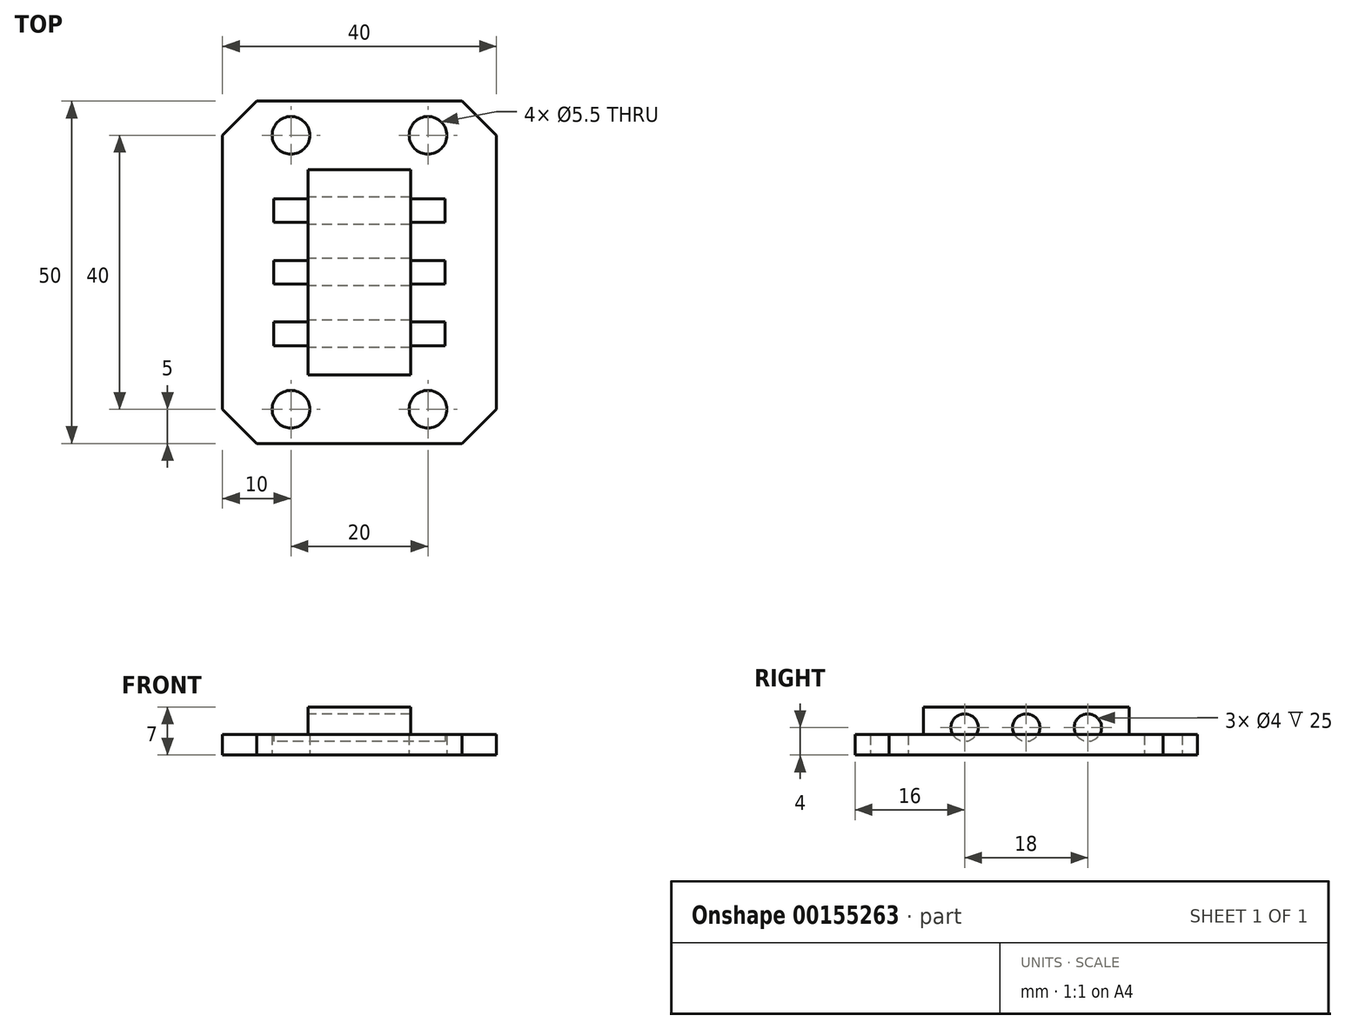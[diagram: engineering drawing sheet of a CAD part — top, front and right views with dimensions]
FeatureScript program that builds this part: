
annotation { "Feature Type Name" : "Feature", "Feature Type Description" : "" }
export const myFeature = defineFeature(function(context is Context, id is Id, definition is map)
    precondition{}
    {
        {
            var Q0;
            Q0=qCreatedBy(makeId("Top.planeOp"),FACE);
            var sketch = newSketch(context, id + "F0", { "sketchPlane" : qUnion([Q0])});
            skLineSegment(sketch, "E0.bottom", {"start": v(20, -25) * mm, "end": v(-20, -25) * mm});
            skLineSegment(sketch, "E0.top", {"start": v(20, 25) * mm, "end": v(-20, 25) * mm});
            skLineSegment(sketch, "E0.left", {"start": v(20, -25) * mm, "end": v(20, 25) * mm});
            skLineSegment(sketch, "E0.right", {"start": v(-20, -25) * mm, "end": v(-20, 25) * mm});
            skPoint(sketch, "E0.middle", {"position": v(0, 0) * mm});
            skLineSegment(sketch, "E1", {"start": v(-10, 25) * mm, "end": v(-10, -25) * mm, "construction": true});
            skLineSegment(sketch, "E2", {"start": v(10, 25) * mm, "end": v(10, -25) * mm, "construction": true});
            skCircle(sketch, "E3", {"center": v(-10, 20) * mm, "radius": 2.75 * mm});
            skCircle(sketch, "E4", {"center": v(10, 20) * mm, "radius": 2.75 * mm});
            skCircle(sketch, "E5.MirrorC", {"center": v(-10, -20) * mm, "radius": 2.75 * mm});
            skCircle(sketch, "E6.MirrorC", {"center": v(10, -20) * mm, "radius": 2.75 * mm});
            skLineSegment(sketch, "E7", {"start": v(0, 25) * mm, "end": v(0, -25) * mm, "construction": true});
            skSolve(sketch);
        }
        {
            var Q0;
            Q0 = qSketchRegion(id + "F0", true);
            extrude(context, id + "F1", {"entities" : qUnion([Q0]), "depth" : 3 * mm});
        }
        {
            var Q0;
            Q0=makeQuery(id+"F1.opExtrude","SWEPT_EDGE",EDGE,{"disambiguationData":[OSD([sQuery(id+"F0.wireOp",EDGE,"E0.top"),sQuery(id+"F0.wireOp",EDGE,"E0.right")])]});
            var Q1;
            Q1=makeQuery(id+"F1.opExtrude","SWEPT_EDGE",EDGE,{"disambiguationData":[OSD([sQuery(id+"F0.wireOp",EDGE,"E0.top"),sQuery(id+"F0.wireOp",EDGE,"E0.left")])]});
            var Q2;
            Q2=makeQuery(id+"F1.opExtrude","SWEPT_EDGE",EDGE,{"disambiguationData":[OSD([sQuery(id+"F0.wireOp",EDGE,"E0.bottom"),sQuery(id+"F0.wireOp",EDGE,"E0.right")])]});
            var Q3;
            Q3=makeQuery(id+"F1.opExtrude","SWEPT_EDGE",EDGE,{"disambiguationData":[OSD([sQuery(id+"F0.wireOp",EDGE,"E0.bottom"),sQuery(id+"F0.wireOp",EDGE,"E0.left")])]});
            chamfer(context, id + "F2", {"entities" : qUnion([Q0, Q1, Q2, Q3]), "width" : 5 * mm, "tangentPropagation" : true});
        }
        {
            var Q0;
            Q0=makeQuery(id+"F1.opExtrude","CAP_FACE",FACE,{"disambiguationData":[OSD([sQuery(id+"F0.wireOp",EDGE,"E0.bottom"),sQuery(id+"F0.wireOp",EDGE,"E0.top"),sQuery(id+"F0.wireOp",EDGE,"E0.left"),sQuery(id+"F0.wireOp",EDGE,"E0.right"),sQuery(id+"F0.wireOp",EDGE,"E3"),sQuery(id+"F0.wireOp",EDGE,"E4"),sQuery(id+"F0.wireOp",EDGE,"E5.MirrorC"),sQuery(id+"F0.wireOp",EDGE,"E6.MirrorC")])],"isStart":false});
            var sketch = newSketch(context, id + "F3", { "sketchPlane" : qUnion([Q0])});
            skLineSegment(sketch, "E8.bottom", {"start": v(7.5, -15) * mm, "end": v(-7.5, -15) * mm});
            skLineSegment(sketch, "E8.top", {"start": v(7.5, 15) * mm, "end": v(-7.5, 15) * mm});
            skLineSegment(sketch, "E8.left", {"start": v(7.5, -15) * mm, "end": v(7.5, 15) * mm});
            skLineSegment(sketch, "E8.right", {"start": v(-7.5, -15) * mm, "end": v(-7.5, 15) * mm});
            skPoint(sketch, "E8.middle", {"position": v(0, 0) * mm});
            skSolve(sketch);
        }
        {
            var Q0;
            Q0 = qSketchRegion(id + "F3", true);
            extrude(context, id + "F4", {"entities" : qUnion([Q0]), "operationType" : NewBodyOperationType.ADD, "depth" : 4 * mm});
        }
        {
            var Q0;
            Q0=qCreatedBy(makeId("Right.planeOp"),FACE);
            var sketch = newSketch(context, id + "F5", { "sketchPlane" : qUnion([Q0])});
            skLineSegment(sketch, "E9", {"start": v(21.14, 4) * mm, "end": v(-25.79, 4) * mm});
            skCircle(sketch, "E10", {"center": v(9, 4) * mm, "radius": 2 * mm});
            skCircle(sketch, "E11", {"center": v(0, 4) * mm, "radius": 2 * mm});
            skCircle(sketch, "E12", {"center": v(-9, 4) * mm, "radius": 2 * mm});
            skSolve(sketch);
        }
        {
            var Q0;
            Q0 = qSketchRegion(id + "F5", true);
            extrude(context, id + "F6", {"entities" : qUnion([Q0]), "operationType" : NewBodyOperationType.REMOVE, "endBound" : BoundingType.SYMMETRIC, "depth" : 25 * mm});
        }
    });
